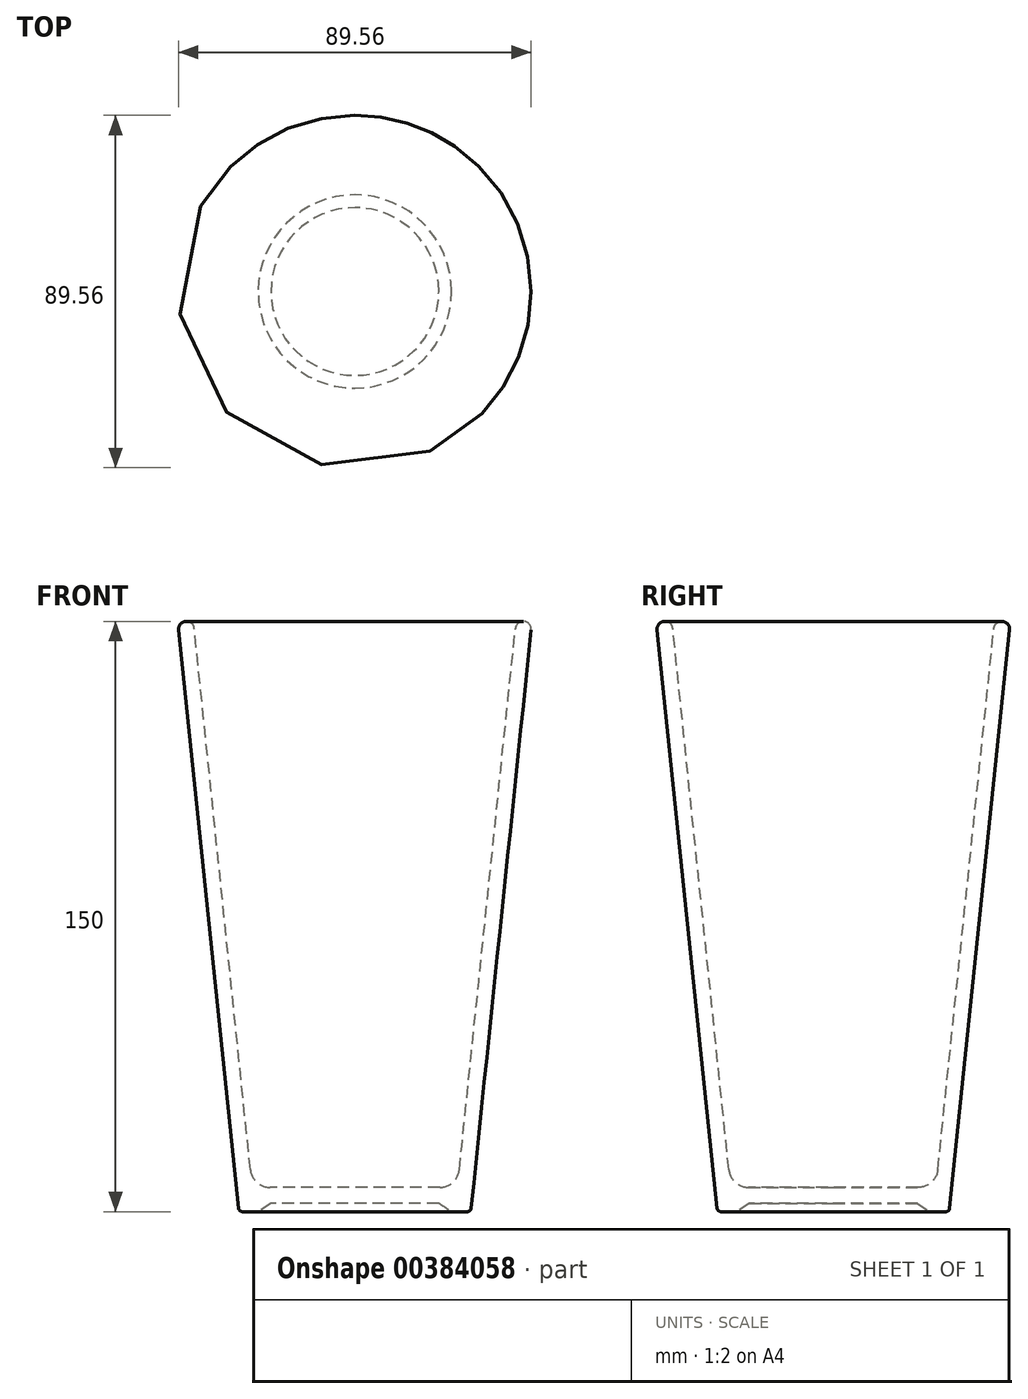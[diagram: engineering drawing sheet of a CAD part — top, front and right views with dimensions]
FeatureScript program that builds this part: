
annotation { "Feature Type Name" : "Feature", "Feature Type Description" : "" }
export const myFeature = defineFeature(function(context is Context, id is Id, definition is map)
    precondition{}
    {
        {
            var Q0;
            Q0=qCreatedBy(makeId("Front.planeOp"),FACE);
            var sketch = newSketch(context, id + "F0", { "sketchPlane" : qUnion([Q0])});
            skLineSegment(sketch, "E0.left", {"start": v(0, 6.17) * mm, "end": v(0, 2.17) * mm});
            skLineSegment(sketch, "E1", {"start": v(-21.32, 2.17) * mm, "end": v(0, 2.17) * mm});
            skLineSegment(sketch, "E2", {"start": v(-28.56, 0) * mm, "end": v(-24.56, 0) * mm});
            skLineSegment(sketch, "E3", {"start": v(-29.55, 0.9) * mm, "end": v(-44.77, 147.8) * mm});
            skLineSegment(sketch, "E4.0", {"start": v(-21.57, 6.17) * mm, "end": v(0, 6.17) * mm});
            skLineSegment(sketch, "E4.3", {"start": v(-26.54, 10.65) * mm, "end": v(-40.8, 148.2) * mm});
            skArc(sketch, "E5", {"start": v(-26.54, 10.65) * mm, "mid": v(-24.92, 7.46) * mm, "end": v(-21.57, 6.17) * mm});
            skArc(sketch, "E6", {"start": v(-40.8, 148.2) * mm, "mid": v(-42.99, 149.99) * mm, "end": v(-44.77, 147.8) * mm});
            skPoint(sketch, "E7.visualSharp", {"position": v(-29.46, 0) * mm});
            skArc(sketch, "E7.filletArc", {"start": v(-29.55, 0.9) * mm, "mid": v(-29.23, 0.26) * mm, "end": v(-28.56, 0) * mm});
            skLineSegment(sketch, "E8", {"start": v(-24.56, 0) * mm, "end": v(-21.32, 2.17) * mm});
            skSolve(sketch);
        }
        {
            var Q0;
            Q0 = qSketchRegion(id + "F0", true);
            var Q1;
            Q1=sQuery(id+"F0.wireOp",EDGE,"E0.left");
            revolve(context, id + "F1", {"entities" : qUnion([Q0]), "axis" : qUnion([Q1]), "revolveType" : RevolveType.FULL});
        }
    });
